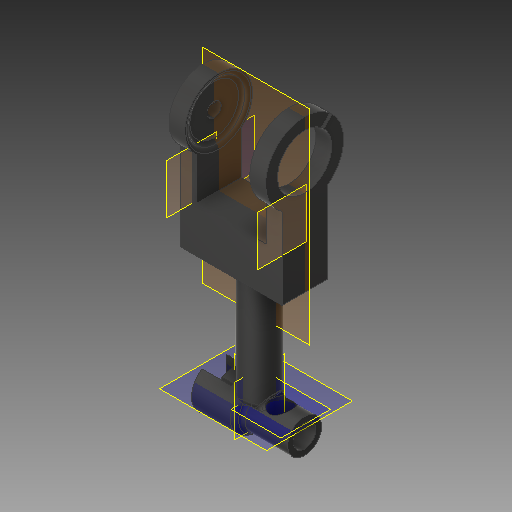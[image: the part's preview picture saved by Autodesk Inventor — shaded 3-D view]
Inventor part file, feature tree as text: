
AUTODESK INVENTOR PART (.ipt)
format: ipt  version: 2018 (Build 220112000, 112)  size: 605,696 bytes
history: native  units: mm
features: extrude x24, sketch x24, plane x8, other x6, fillet x4
ambient origin geometry x8: Origin, YZ Plane, XZ Plane, XY Plane, X Axis, Y Axis, Z Axis, Center Point
bodies: Body1 (feature_tree)
feature tree (66):
  other  "Sólido1"
  extrude  "Extrusión1"  Depth=20.0mm
  plane  "Plano de trabajo1"
  plane  "Plano de trabajo2"
  extrude  "Extrusión8"  Depth=24.5mm
  plane  "Plano de trabajo5"
  plane  "Plano de trabajo6"
  extrude  "Extrusión12"  Depth=10.0mm TaperAngle=0.0deg
  extrude  "Extrusión13"  Depth=6.3mm
  extrude  "Extrusión14"  Depth=24.5mm
  extrude  "Extrusión15"  Depth=1.6mm
  extrude  "Extrusión16"  Depth=4.0mm
  extrude  "Extrusión23"  Depth=20.0mm
  extrude  "Extrusión27"  Depth=10.0mm
  extrude  "Extrusión28"  Depth=25.0mm TaperAngle=0.0deg
  extrude  "Extrusión29"  Depth=10.0mm TaperAngle=0.0deg
  extrude  "Extrusión30"  Depth=50.0mm TaperAngle=0.0deg
  plane  "Plano de trabajo7"
  plane  "Plano de trabajo8"
  plane  "Plano de trabajo9"
  extrude  "Extrusión31"  Depth=20.0mm TaperAngle=0.0deg
  extrude  "Extrusión32"  Depth=20.0mm TaperAngle=0.0deg
  sketch  "Boceto40"  dims[d145=2.0mm d146=2.0mm d147=3.9mm]
  sketch  "Boceto41"  dims[d148=2.0mm d149=3.9mm d150=7.9mm d151=0.0mm]
  extrude  "Extrusión35"  Depth=2.0mm
  fillet  "Empalme6"  Radius=3.9mm
  extrude  "Extrusion37"  Depth=3.9mm
  plane  "Plano de trabajo10"
  sketch  "Sketch45"  dims[d159=10.0mm d160=0.0mm d161=5.5mm]
  other  "Edición directa1"
  fillet  "Empalme8"  Radius=7.9mm
  extrude  "Extrusión40"  Depth=10.0mm
  extrude  "Extrusión41"  Depth=10.0mm
  extrude  "Extrusión42"  Depth=10.0mm
  extrude  "Extrusión43"  TaperAngle=0.0deg  [1 undecoded]
  extrude  "Extrusión44"  Depth=30.0mm TaperAngle=0.0deg
  extrude  "Extrusión45"  Depth=24.0mm
  extrude  "Extrusión46"  Depth=0.5mm
  fillet  "Empalme9"  Radius=0.5mm
  fillet  "Empalme10"  Radius=7.9mm
  extrude  "Extrusión47"  Depth=5.9mm
  sketch  "Boceto1"  dims[d0=40.0mm d1=20.0mm]
  sketch  "Boceto8"  dims[d2=5.0mm d3=0.0mm d28=24.5mm]
  sketch  "Boceto17"  dims[d30=10.0mm d31=0.0mm d53=5.0mm d54=0.0mm]
  sketch  "Boceto18"  dims[d55=3.0mm d56=0.0mm d58=6.3mm]
  sketch  "Boceto19"  dims[d59=8.0mm d60=0.0mm d61=24.5mm]
  sketch  "Boceto20"  dims[d62=5.0mm d63=0.0mm d64=1.6mm]
  sketch  "Boceto21"  dims[d65=2.0mm d66=0.0mm d99=4.0mm]
  sketch  "Boceto28"  dims[d100=25.0mm d101=0.0mm d117=20.0mm]
  sketch  "Boceto32"  dims[d118=90.0deg d119=10.0mm]
  sketch  "Boceto33"  dims[d120=5.0mm d121=25.0mm d122=0.0mm]
  sketch  "Boceto34"  dims[d123=10.0mm d124=0.0mm d125=20.0mm d126=0.0mm]
  sketch  "Boceto35"  dims[d127=15.0mm d128=50.0mm d129=0.0mm]
  sketch  "Boceto37"  dims[d131=20.0mm d132=20.0mm d133=0.0mm]
  sketch  "Boceto38"  dims[d134=14.8mm d135=20.0mm d136=0.0mm]
  sketch  "Boceto42"  dims[d157=3.0mm d158=10.0mm]
  sketch  "Boceto46"  dims[d162=5.0mm d163=10.0mm]
  sketch  "Boceto47"  dims[d169=0.0mm d170=0.0mm d171=-3.0mm d172=0.0mm d173=0.0mm d174=-3.0mm]
  sketch  "Boceto48"  dims[d175=0.0mm d176=0.0mm d177=2.0mm d178=0.0mm d179=0.0mm d180=30.0mm]
  sketch  "Boceto49"  dims[d181=2.0mm d182=24.0mm]
  sketch  "Boceto50"  dims[d183=7.0mm d184=0.0mm d185=0.5mm d186=0.5mm d187=7.9mm d188=0.0mm]
  sketch  "Boceto51"  dims[d189=7.9mm d190=0.0mm d191=5.9mm d192=0.8mm d193=0.8mm d194=5.0mm d195=0.0mm d196=15.0mm d197=20.0mm d198=0.0mm d199=8.0mm d200=0.0mm d201=3.0mm d202=0.0mm d203=2.0mm d204=2.0mm d207=7.0mm d208=0.0mm]
  other  "Desplazar1"
  other  "Desplazar2"
  other  "Desplazar3"
  other  "Desplazar4"
note: 1 required parameter value undecoded (feature->parameter linkage not recoverable at this tier; creation-order binding heuristic only, values carry confidence <= 0.55)
